# Revit family: RMT230(T)_24(T)_RFA
name_source: partatom
category: Data Devices
units: mm (PartAtom-declared; Revit-internal decimal feet)

## family parameters
Cut with Voids When Loaded = No
Host = Face
Maintain Annotation Orientation = No
Part Type = Normal
Room Calculation Point = No
Round Connector Dimension = Use Diameter
Shared = No

## types (5) — shared parameters
Ball Pressure Test = 75
Body Material = Danfoss Plastic White
Default Elevation = 1219.2 mm  [stored 4 ft]
Description = Room Thermostat
IP Rating = IP20
IfcExportAs = IfcElectricApplianceType
L1 = 78 mm  [stored 0.255906 ft]
L2 = 47.5 mm
L3 = 30.52 mm  [stored 0.100131 ft]
LOD 200 = No
LOD 350 = Yes
Manufacturer = Danfoss
Max Temperature Setting = 30 °C
Min Temperature Setting = 8 °C
Operating Temperature Range = -10 - +50 °C
Switch Type = SPDT
URL = https://store.danfoss.com
Weight = 0.15 kg

## per-type parameters (varying)
| type | Accelerator | Built-in Thermometer | IfcExportType | Model | Model Type | Night Set Back | Power Supply RT | Switch Rating | Voltage |
| RMT230_230V_087N1100 | Parallel | No | RMT230 | 087N1100 | RMT230_230V | No | 230 V | 10 A (4 A) at 230 VAC | 230 V |
| RMT230_230V_No Accelerator Heater_087N1110 | No | No | RMT230 | 087N1110 | RMT230_230V_No Accelerator Heater | No | 230 V | 10 A (4 A) at 230 VAC | 230 V |
| RMT24_24V_087N1196 | Parallel | No | RMT24 | 087N1196 | RMT24_24V | No | 24 V | 10 A (4 A) at 24 VAC | 24 V |
| RMT24T_24V_087N1197 | Parallel | Yes | RMT24T | 087N1197 | RMT24T_24V | Yes | 24 V | 10 A (4 A) at 24 VAC | 24 V |
| RMT230T_230V_087N1125 | Parallel | Yes | RMT230T | 087N1125 | RMT230T_230V | Yes | 230 V | 10 A (4 A) at 230 VAC | 230 V |

note: source unit labels omitted for Ball Pressure Test — the stored unit's dimension contradicts the parameter name (converter mislabeling)

note: [stored X ft] marks values corroborated as IEEE doubles in the binary element streams (Revit-internal decimal feet)

## geometry (parser evidence)
native form markers: Sweep x2
no freeform markers — native parametric forms only
